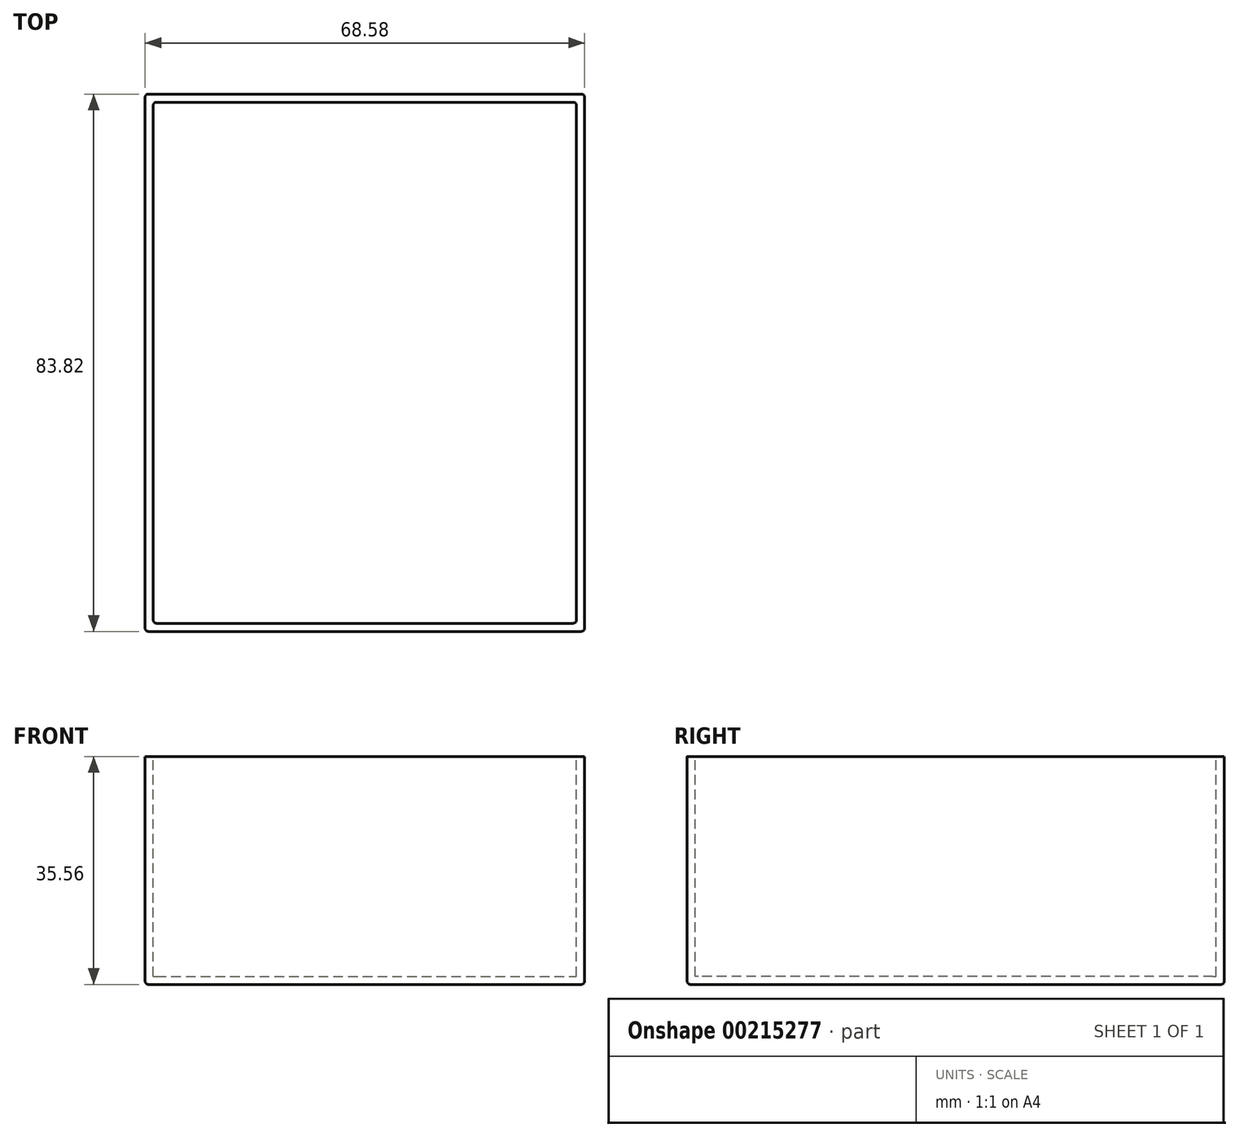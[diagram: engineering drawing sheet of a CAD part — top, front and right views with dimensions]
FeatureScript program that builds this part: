
annotation { "Feature Type Name" : "Feature", "Feature Type Description" : "" }
export const myFeature = defineFeature(function(context is Context, id is Id, definition is map)
    precondition{}
    {
        {
            var Q0;
            Q0=qCreatedBy(makeId("Top.planeOp"),FACE);
            var sketch = newSketch(context, id + "F0", { "sketchPlane" : qUnion([Q0])});
            skLineSegment(sketch, "E0.bottom", {"start": v(2.54, 2.54) * mm, "end": v(71.12, 2.54) * mm});
            skLineSegment(sketch, "E0.top", {"start": v(2.54, 86.36) * mm, "end": v(71.12, 86.36) * mm});
            skLineSegment(sketch, "E0.left", {"start": v(2.54, 2.54) * mm, "end": v(2.54, 86.36) * mm});
            skLineSegment(sketch, "E0.right", {"start": v(71.12, 2.54) * mm, "end": v(71.12, 86.36) * mm});
            skSolve(sketch);
        }
        {
            var Q0;
            Q0 = qSketchRegion(id + "F0", true);
            extrude(context, id + "F1", {"entities" : qUnion([Q0]), "depth" : 35.56 * mm});
        }
        {
            var Q0;
            Q0=makeQuery(id+"F1.opExtrude","SWEPT_EDGE",EDGE,{"disambiguationData":[OSD([sQuery(id+"F0.wireOp",EDGE,"E0.bottom"),sQuery(id+"F0.wireOp",EDGE,"E0.right")])]});
            var Q1;
            Q1=makeQuery(id+"F1.opExtrude","SWEPT_EDGE",EDGE,{"disambiguationData":[OSD([sQuery(id+"F0.wireOp",EDGE,"E0.top"),sQuery(id+"F0.wireOp",EDGE,"E0.right")])]});
            var Q2;
            Q2=makeQuery(id+"F1.opExtrude","SWEPT_EDGE",EDGE,{"disambiguationData":[OSD([sQuery(id+"F0.wireOp",EDGE,"E0.bottom"),sQuery(id+"F0.wireOp",EDGE,"E0.left")])]});
            var Q3;
            Q3=makeQuery(id+"F1.opExtrude","SWEPT_EDGE",EDGE,{"disambiguationData":[OSD([sQuery(id+"F0.wireOp",EDGE,"E0.top"),sQuery(id+"F0.wireOp",EDGE,"E0.left")])]});
            var Q4;
            Q4=makeQuery(id+"F1.opExtrude","CAP_EDGE",EDGE,{"disambiguationData":[OSD([sQuery(id+"F0.wireOp",EDGE,"E0.right")])],"isStart":true});
            var Q5;
            Q5=makeQuery(id+"F1.opExtrude","CAP_FACE",FACE,{"disambiguationData":[OSD([sQuery(id+"F0.wireOp",EDGE,"E0.bottom"),sQuery(id+"F0.wireOp",EDGE,"E0.top"),sQuery(id+"F0.wireOp",EDGE,"E0.left"),sQuery(id+"F0.wireOp",EDGE,"E0.right")])],"isStart":true});
            var Q6;
            Q6=makeQuery(id+"F1.opExtrude","CAP_EDGE",EDGE,{"disambiguationData":[OSD([sQuery(id+"F0.wireOp",EDGE,"E0.left")])],"isStart":true});
            var Q7;
            Q7=makeQuery(id+"F1.opExtrude","CAP_EDGE",EDGE,{"disambiguationData":[OSD([sQuery(id+"F0.wireOp",EDGE,"E0.top")])],"isStart":true});
            fillet(context, id + "F2", {"entities" : qUnion([Q0, Q1, Q2, Q3, Q4, Q5, Q6, Q7]), "radius" : 0.5 * mm, "tangentPropagation" : true, "allowEdgeOverflow" : false});
        }
        {
            var Q0;
            Q0=makeQuery(id+"F1.opExtrude","CAP_FACE",FACE,{"disambiguationData":[OSD([sQuery(id+"F0.wireOp",EDGE,"E0.bottom"),sQuery(id+"F0.wireOp",EDGE,"E0.top"),sQuery(id+"F0.wireOp",EDGE,"E0.left"),sQuery(id+"F0.wireOp",EDGE,"E0.right")])],"isStart":false});
            shell(context, id + "F3", {"entities" : qUnion([Q0]), "thickness" : 1.27 * mm});
        }
        {
            var Q0;
            Q0=makeQuery(id+"F3.opShell","OFFSET_EDGE",EDGE,{"disambiguationData":[OSD([sQuery(id+"F0.wireOp",EDGE,"E0.bottom"),sQuery(id+"F0.wireOp",EDGE,"E0.right")])]});
            var Q1;
            Q1=makeQuery(id+"F3.opShell","OFFSET_EDGE",EDGE,{"disambiguationData":[OSD([sQuery(id+"F0.wireOp",EDGE,"E0.top"),sQuery(id+"F0.wireOp",EDGE,"E0.right")])]});
            var Q2;
            Q2=makeQuery(id+"F3.opShell","OFFSET_EDGE",EDGE,{"disambiguationData":[OSD([sQuery(id+"F0.wireOp",EDGE,"E0.top"),sQuery(id+"F0.wireOp",EDGE,"E0.left")])]});
            var Q3;
            Q3=makeQuery(id+"F3.opShell","OFFSET_EDGE",EDGE,{"disambiguationData":[OSD([sQuery(id+"F0.wireOp",EDGE,"E0.bottom"),sQuery(id+"F0.wireOp",EDGE,"E0.left")])]});
            fillet(context, id + "F4", {"entities" : qUnion([Q0, Q1, Q2, Q3]), "radius" : 0.5 * mm, "tangentPropagation" : true, "allowEdgeOverflow" : false});
        }
    });
